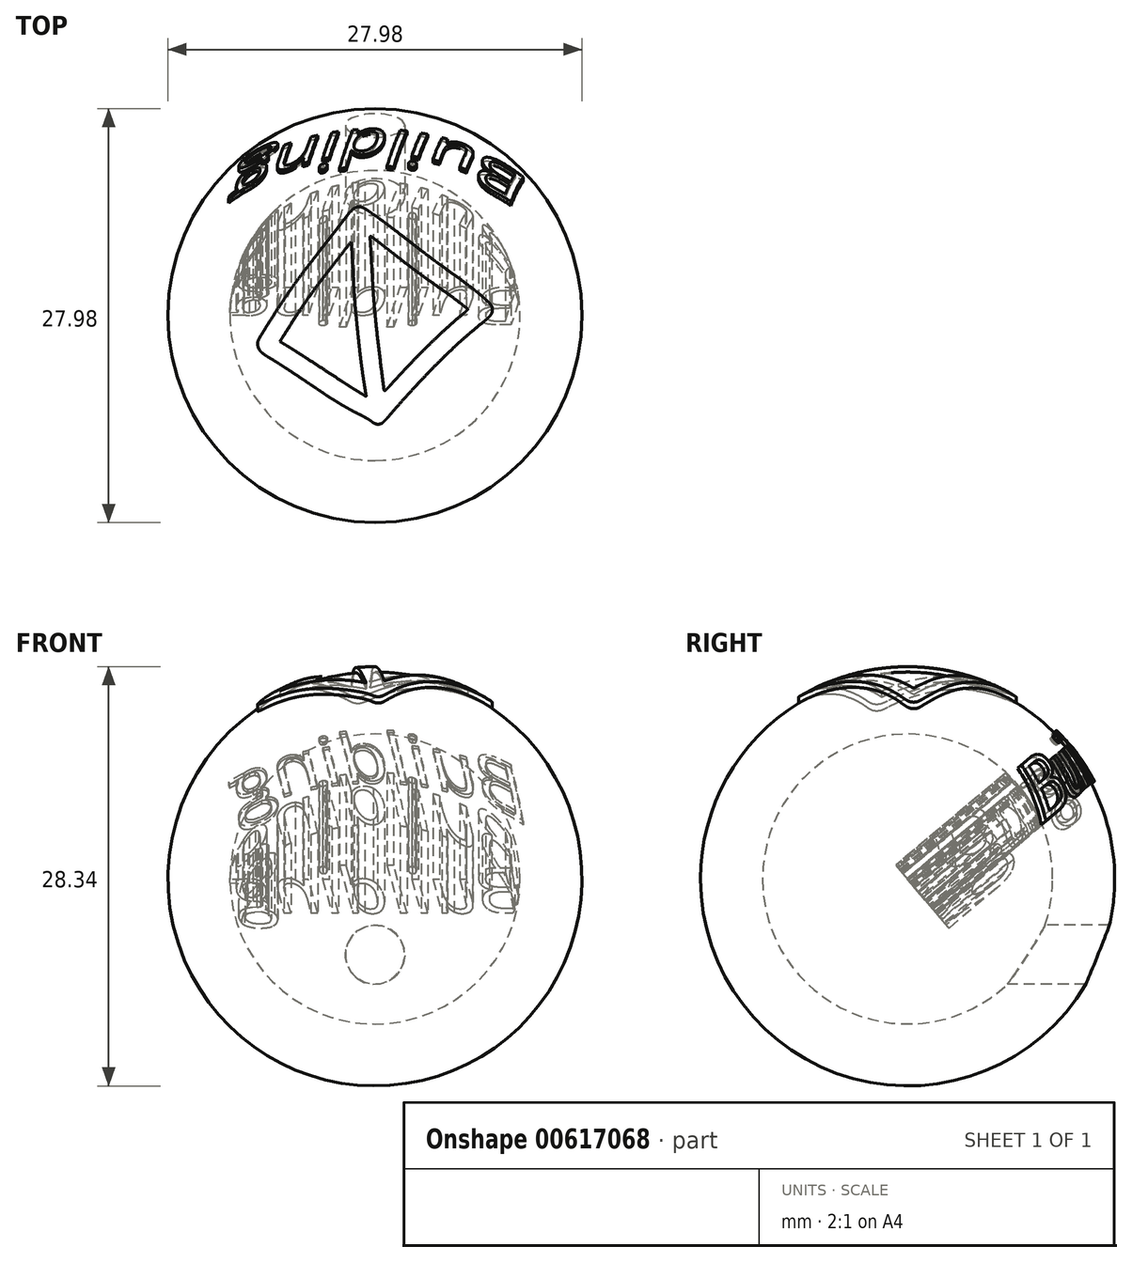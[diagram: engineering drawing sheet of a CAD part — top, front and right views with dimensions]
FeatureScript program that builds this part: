
annotation { "Feature Type Name" : "Feature", "Feature Type Description" : "" }
export const myFeature = defineFeature(function(context is Context, id is Id, definition is map)
    precondition{}
    {
        {
            var Q0;
            Q0=qCreatedBy(makeId("Top.planeOp"),FACE);
            var sketch = newSketch(context, id + "F0", { "sketchPlane" : qUnion([Q0])});
            skLineSegment(sketch, "E0", {"start": v(0, -10) * mm, "end": v(0, 10) * mm});
            skArc(sketch, "E1", {"start": v(0, 10) * mm, "mid": v(-10, 0) * mm, "end": v(0, -10) * mm});
            skSolve(sketch);
        }
        {
            var Q0;
            {var subQ0=sQuery(id+"F0.wireOp",EDGE,"E1");Q0=makeQuery(id+"F0.imprint","IMPRINT",FACE,{"disambiguationData":[TD([[makeQuery(id+"F0.imprint","IMPRINT",EDGE,{"derivedFrom":subQ0}),1.0]])]});}
            var Q1;
            Q1=sQuery(id+"F0.wireOp",EDGE,"E0");
            revolve(context, id + "F1", {"entities" : qUnion([Q0]), "axis" : qUnion([Q1]), "revolveType" : RevolveType.FULL});
        }
        {
            var Q0;
            Q0=makeQuery(id+"F1.opRevolve","SWEPT_BODY",BODY,{"disambiguationData":[OSD([sQuery(id+"F0.wireOp",EDGE,"E0"),sQuery(id+"F0.wireOp",EDGE,"E1")])]});
            var Q1;
            Q1=sQuery(id+"F0.wireOp",VERTEX,"NPe4G0ez-t7S9-9isL-QO5v-uuJu600mHcIT.center");
            var Q2;
            Q2=sQuery(id+"F0.wireOp",VERTEX,"E1.center");
            transform(context, id + "F2", {"entities" : qUnion([Q0]), "transformType" : TransformType.SCALE_UNIFORMLY, "scale" : 33.3, "scalePoint" : qUnion([Q2]), "makeCopy" : false});
        }
        {
            var Q0;
            Q0=qCreatedBy(makeId("Top.planeOp"),FACE);
            var sketch = newSketch(context, id + "F3", { "sketchPlane" : qUnion([Q0])});
            skArc(sketch, "E2", {"start": v(-33, 172.81) * mm, "mid": v(-34.37, 171.98) * mm, "end": v(-35.66, 171) * mm});
            skArc(sketch, "E3", {"start": v(-35.66, 171) * mm, "mid": v(-37.15, 169.67) * mm, "end": v(-38.56, 168.26) * mm});
            skArc(sketch, "E4", {"start": v(-38.56, 168.26) * mm, "mid": v(-40.37, 166.25) * mm, "end": v(-42.1, 164.18) * mm});
            skArc(sketch, "E5", {"start": v(-42.1, 164.18) * mm, "mid": v(-44.55, 161.1) * mm, "end": v(-46.95, 157.98) * mm});
            skArc(sketch, "E6", {"start": v(-46.95, 157.98) * mm, "mid": v(-49.6, 154.52) * mm, "end": v(-52.25, 151.08) * mm});
            skArc(sketch, "E7", {"start": v(-52.25, 151.08) * mm, "mid": v(-56.88, 145.1) * mm, "end": v(-61.52, 139.12) * mm});
            skArc(sketch, "E8", {"start": v(-61.52, 139.12) * mm, "mid": v(-66.9, 132.2) * mm, "end": v(-72.28, 125.28) * mm});
            skArc(sketch, "E9", {"start": v(-72.28, 125.28) * mm, "mid": v(-77.76, 118.26) * mm, "end": v(-83.25, 111.24) * mm});
            skArc(sketch, "E10", {"start": v(-83.25, 111.24) * mm, "mid": v(-97.95, 92.31) * mm, "end": v(-112.54, 73.3) * mm});
            skArc(sketch, "E11", {"start": v(-112.54, 73.3) * mm, "mid": v(-122.82, 59.57) * mm, "end": v(-132.87, 45.67) * mm});
            skArc(sketch, "E12", {"start": v(-132.87, 45.67) * mm, "mid": v(-142, 32.54) * mm, "end": v(-150.9, 19.25) * mm});
            skArc(sketch, "E13", {"start": v(-150.9, 19.25) * mm, "mid": v(-161.66, 2.63) * mm, "end": v(-172.26, -14.1) * mm});
            skArc(sketch, "E14", {"start": v(-172.26, -14.1) * mm, "mid": v(-177.97, -23.22) * mm, "end": v(-183.64, -32.36) * mm});
            skArc(sketch, "E15", {"start": v(-183.64, -32.36) * mm, "mid": v(-185.48, -35.48) * mm, "end": v(-187.18, -38.67) * mm});
            skArc(sketch, "E16", {"start": v(-187.18, -38.67) * mm, "mid": v(-188, -40.65) * mm, "end": v(-188.56, -42.72) * mm});
            skArc(sketch, "E17", {"start": v(-188.56, -42.72) * mm, "mid": v(-188.82, -44.8) * mm, "end": v(-188.77, -46.88) * mm});
            skArc(sketch, "E18", {"start": v(-188.77, -46.88) * mm, "mid": v(-188.23, -49.88) * mm, "end": v(-187.2, -52.73) * mm});
            skArc(sketch, "E19", {"start": v(-187.2, -52.73) * mm, "mid": v(-185.68, -55.44) * mm, "end": v(-183.75, -57.87) * mm});
            skArc(sketch, "E20", {"start": v(-183.75, -57.87) * mm, "mid": v(-180.92, -60.6) * mm, "end": v(-177.8, -63) * mm});
            skArc(sketch, "E21", {"start": v(-177.8, -63) * mm, "mid": v(-173.08, -66.1) * mm, "end": v(-168.25, -69) * mm});
            skArc(sketch, "E22", {"start": v(-168.25, -69) * mm, "mid": v(-164.73, -71.07) * mm, "end": v(-161.26, -73.21) * mm});
            skArc(sketch, "E23", {"start": v(-161.26, -73.21) * mm, "mid": v(-155.32, -76.99) * mm, "end": v(-149.4, -80.79) * mm});
            skArc(sketch, "E24", {"start": v(-149.4, -80.79) * mm, "mid": v(-142.56, -85.22) * mm, "end": v(-135.75, -89.69) * mm});
            skArc(sketch, "E25", {"start": v(-135.75, -89.69) * mm, "mid": v(-128.86, -94.25) * mm, "end": v(-122, -98.84) * mm});
            skArc(sketch, "E26", {"start": v(-122, -98.84) * mm, "mid": v(-115.2, -103.41) * mm, "end": v(-108.4, -107.98) * mm});
            skArc(sketch, "E27", {"start": v(-108.4, -107.98) * mm, "mid": v(-101.82, -112.4) * mm, "end": v(-95.25, -116.8) * mm});
            skArc(sketch, "E28", {"start": v(-95.25, -116.8) * mm, "mid": v(-89.63, -120.57) * mm, "end": v(-84.02, -124.33) * mm});
            skArc(sketch, "E29", {"start": v(-84.02, -124.33) * mm, "mid": v(-81, -126.34) * mm, "end": v(-78, -128.35) * mm});
            skArc(sketch, "E30", {"start": v(-78, -128.35) * mm, "mid": v(-71.4, -132.67) * mm, "end": v(-64.72, -136.88) * mm});
            skArc(sketch, "E31", {"start": v(-64.72, -136.88) * mm, "mid": v(-57.8, -141.12) * mm, "end": v(-50.8, -145.26) * mm});
            skArc(sketch, "E32", {"start": v(-50.8, -145.26) * mm, "mid": v(-44.03, -149.14) * mm, "end": v(-37.21, -152.92) * mm});
            skArc(sketch, "E33", {"start": v(-37.21, -152.92) * mm, "mid": v(-31.14, -156.15) * mm, "end": v(-25, -159.25) * mm});
            skArc(sketch, "E34", {"start": v(-25, -159.25) * mm, "mid": v(-22.06, -160.7) * mm, "end": v(-19.16, -162.22) * mm});
            skArc(sketch, "E35", {"start": v(-19.16, -162.22) * mm, "mid": v(-16.38, -163.71) * mm, "end": v(-13.63, -165.25) * mm});
            skArc(sketch, "E36", {"start": v(-13.63, -165.25) * mm, "mid": v(-11.31, -166.6) * mm, "end": v(-9.01, -168) * mm});
            skArc(sketch, "E37", {"start": v(-9.01, -168) * mm, "mid": v(-7.81, -168.8) * mm, "end": v(-6.69, -169.7) * mm});
            skArc(sketch, "E38", {"start": v(-6.69, -169.7) * mm, "mid": v(-4.48, -171.46) * mm, "end": v(-2.12, -173) * mm});
            skArc(sketch, "E39", {"start": v(-2.12, -173) * mm, "mid": v(0.04, -174.03) * mm, "end": v(2.34, -174.72) * mm});
            skArc(sketch, "E40", {"start": v(2.34, -174.72) * mm, "mid": v(4.5, -174.99) * mm, "end": v(6.69, -174.86) * mm});
            skArc(sketch, "E41", {"start": v(6.69, -174.86) * mm, "mid": v(8.87, -174.35) * mm, "end": v(10.94, -173.5) * mm});
            skArc(sketch, "E42", {"start": v(10.94, -173.5) * mm, "mid": v(11.75, -173) * mm, "end": v(12.5, -172.4) * mm});
            skArc(sketch, "E43", {"start": v(12.5, -172.4) * mm, "mid": v(13.95, -171) * mm, "end": v(15.38, -169.59) * mm});
            skArc(sketch, "E44", {"start": v(15.38, -169.59) * mm, "mid": v(17.06, -167.86) * mm, "end": v(18.7, -166.1) * mm});
            skArc(sketch, "E45", {"start": v(18.7, -166.1) * mm, "mid": v(20.42, -164.19) * mm, "end": v(22.1, -162.24) * mm});
            skArc(sketch, "E46", {"start": v(22.1, -162.24) * mm, "mid": v(32.46, -150.21) * mm, "end": v(42.96, -138.3) * mm});
            skArc(sketch, "E47", {"start": v(42.96, -138.3) * mm, "mid": v(54.31, -125.7) * mm, "end": v(65.78, -113.23) * mm});
            skArc(sketch, "E48", {"start": v(65.78, -113.23) * mm, "mid": v(77.16, -101.09) * mm, "end": v(88.65, -89.06) * mm});
            skArc(sketch, "E49", {"start": v(88.65, -89.06) * mm, "mid": v(99.07, -78.41) * mm, "end": v(109.64, -67.9) * mm});
            skArc(sketch, "E50", {"start": v(109.64, -67.9) * mm, "mid": v(117.81, -59.96) * mm, "end": v(126.06, -52.09) * mm});
            skArc(sketch, "E51", {"start": v(126.06, -52.09) * mm, "mid": v(133.02, -45.6) * mm, "end": v(140.08, -39.23) * mm});
            skArc(sketch, "E52", {"start": v(140.08, -39.23) * mm, "mid": v(147.61, -32.64) * mm, "end": v(155.23, -26.15) * mm});
            skArc(sketch, "E53", {"start": v(155.23, -26.15) * mm, "mid": v(165.3, -17.77) * mm, "end": v(175.42, -9.46) * mm});
            skArc(sketch, "E54", {"start": v(175.42, -9.46) * mm, "mid": v(179.05, -6.39) * mm, "end": v(182.58, -3.2) * mm});
            skArc(sketch, "E55", {"start": v(182.58, -3.2) * mm, "mid": v(184.71, -0.94) * mm, "end": v(186.58, 1.54) * mm});
            skArc(sketch, "E56", {"start": v(186.58, 1.54) * mm, "mid": v(187.71, 3.63) * mm, "end": v(188.46, 5.89) * mm});
            skArc(sketch, "E57", {"start": v(188.46, 5.89) * mm, "mid": v(188.81, 8.25) * mm, "end": v(188.75, 10.64) * mm});
            skArc(sketch, "E58", {"start": v(188.75, 10.64) * mm, "mid": v(188.42, 12.49) * mm, "end": v(187.86, 14.28) * mm});
            skArc(sketch, "E59", {"start": v(187.86, 14.28) * mm, "mid": v(187.09, 15.92) * mm, "end": v(186.1, 17.44) * mm});
            skArc(sketch, "E60", {"start": v(186.1, 17.44) * mm, "mid": v(184.48, 19.41) * mm, "end": v(182.72, 21.24) * mm});
            skArc(sketch, "E61", {"start": v(182.72, 21.24) * mm, "mid": v(179.3, 24.49) * mm, "end": v(175.84, 27.68) * mm});
            skArc(sketch, "E62", {"start": v(175.84, 27.68) * mm, "mid": v(171.1, 31.88) * mm, "end": v(166.27, 35.95) * mm});
            skArc(sketch, "E63", {"start": v(166.27, 35.95) * mm, "mid": v(160.23, 40.83) * mm, "end": v(154.12, 45.63) * mm});
            skArc(sketch, "E64", {"start": v(154.12, 45.63) * mm, "mid": v(146.93, 51.13) * mm, "end": v(139.67, 56.53) * mm});
            skArc(sketch, "E65", {"start": v(139.67, 56.53) * mm, "mid": v(131.36, 62.6) * mm, "end": v(123, 68.58) * mm});
            skArc(sketch, "E66", {"start": v(123, 68.58) * mm, "mid": v(114.4, 74.72) * mm, "end": v(105.83, 80.91) * mm});
            skArc(sketch, "E67", {"start": v(105.83, 80.91) * mm, "mid": v(98.5, 86.27) * mm, "end": v(91.21, 91.69) * mm});
            skArc(sketch, "E68", {"start": v(91.21, 91.69) * mm, "mid": v(83.18, 97.75) * mm, "end": v(75.19, 103.87) * mm});
            skArc(sketch, "E69", {"start": v(75.19, 103.87) * mm, "mid": v(64.09, 112.45) * mm, "end": v(53, 121.05) * mm});
            skArc(sketch, "E70", {"start": v(53, 121.05) * mm, "mid": v(42.99, 128.83) * mm, "end": v(32.94, 136.58) * mm});
            skArc(sketch, "E71", {"start": v(32.94, 136.58) * mm, "mid": v(25.36, 142.38) * mm, "end": v(17.73, 148.12) * mm});
            skArc(sketch, "E72", {"start": v(17.73, 148.12) * mm, "mid": v(11.29, 152.88) * mm, "end": v(4.8, 157.6) * mm});
            skArc(sketch, "E73", {"start": v(4.8, 157.6) * mm, "mid": v(-1.5, 162.08) * mm, "end": v(-7.86, 166.51) * mm});
            skArc(sketch, "E74", {"start": v(-7.86, 166.51) * mm, "mid": v(-12.3, 169.46) * mm, "end": v(-16.82, 172.26) * mm});
            skArc(sketch, "E75", {"start": v(-16.82, 172.26) * mm, "mid": v(-19.64, 173.67) * mm, "end": v(-22.64, 174.66) * mm});
            skArc(sketch, "E76", {"start": v(-22.64, 174.66) * mm, "mid": v(-25.1, 175) * mm, "end": v(-27.56, 174.77) * mm});
            skArc(sketch, "E77", {"start": v(-27.56, 174.77) * mm, "mid": v(-30.35, 173.98) * mm, "end": v(-33, 172.81) * mm});
            skArc(sketch, "E78", {"start": v(2.5, 120.65) * mm, "mid": v(4.7, 119) * mm, "end": v(6.88, 117.32) * mm});
            skArc(sketch, "E79", {"start": v(6.88, 117.32) * mm, "mid": v(10.53, 114.5) * mm, "end": v(14.18, 111.67) * mm});
            skArc(sketch, "E80", {"start": v(14.18, 111.67) * mm, "mid": v(18.38, 108.4) * mm, "end": v(22.57, 105.14) * mm});
            skArc(sketch, "E81", {"start": v(22.57, 105.14) * mm, "mid": v(26.8, 101.84) * mm, "end": v(31, 98.53) * mm});
            skArc(sketch, "E82", {"start": v(31, 98.53) * mm, "mid": v(40.47, 91.14) * mm, "end": v(49.96, 83.78) * mm});
            skArc(sketch, "E83", {"start": v(49.96, 83.78) * mm, "mid": v(57.43, 78.07) * mm, "end": v(64.95, 72.41) * mm});
            skArc(sketch, "E84", {"start": v(64.95, 72.41) * mm, "mid": v(72.33, 66.96) * mm, "end": v(79.75, 61.57) * mm});
            skArc(sketch, "E85", {"start": v(79.75, 61.57) * mm, "mid": v(88.87, 55.05) * mm, "end": v(98, 48.58) * mm});
            skArc(sketch, "E86", {"start": v(98, 48.58) * mm, "mid": v(108.94, 40.81) * mm, "end": v(119.82, 32.97) * mm});
            skArc(sketch, "E87", {"start": v(119.82, 32.97) * mm, "mid": v(127.9, 27) * mm, "end": v(135.87, 20.91) * mm});
            skArc(sketch, "E88", {"start": v(135.87, 20.91) * mm, "mid": v(142.08, 16.05) * mm, "end": v(148.26, 11.14) * mm});
            skArc(sketch, "E89", {"start": v(148.26, 11.14) * mm, "mid": v(148.87, 10.2) * mm, "end": v(148.8, 9.07) * mm});
            skArc(sketch, "E90", {"start": v(148.8, 9.07) * mm, "mid": v(148.66, 8.82) * mm, "end": v(148.47, 8.6) * mm});
            skArc(sketch, "E91", {"start": v(148.47, 8.6) * mm, "mid": v(147.14, 7.42) * mm, "end": v(145.8, 6.25) * mm});
            skArc(sketch, "E92", {"start": v(145.8, 6.25) * mm, "mid": v(144.24, 4.89) * mm, "end": v(142.67, 3.54) * mm});
            skArc(sketch, "E93", {"start": v(142.67, 3.54) * mm, "mid": v(140.84, 2) * mm, "end": v(139, 0.47) * mm});
            skArc(sketch, "E94", {"start": v(139, 0.47) * mm, "mid": v(126.28, -10.36) * mm, "end": v(113.83, -21.52) * mm});
            skArc(sketch, "E95", {"start": v(113.83, -21.52) * mm, "mid": v(99.63, -34.82) * mm, "end": v(85.65, -48.36) * mm});
            skArc(sketch, "E96", {"start": v(85.65, -48.36) * mm, "mid": v(70.67, -63.33) * mm, "end": v(55.94, -78.53) * mm});
            skArc(sketch, "E97", {"start": v(55.94, -78.53) * mm, "mid": v(40.89, -94.52) * mm, "end": v(26.07, -110.7) * mm});
            skArc(sketch, "E98", {"start": v(26.07, -110.7) * mm, "mid": v(24.28, -112.68) * mm, "end": v(22.47, -114.64) * mm});
            skArc(sketch, "E99", {"start": v(22.47, -114.64) * mm, "mid": v(20.9, -116.3) * mm, "end": v(19.32, -117.95) * mm});
            skArc(sketch, "E100", {"start": v(19.32, -117.95) * mm, "mid": v(17.95, -119.36) * mm, "end": v(16.56, -120.76) * mm});
            skArc(sketch, "E101", {"start": v(16.56, -120.76) * mm, "mid": v(16.35, -120.9) * mm, "end": v(16.1, -120.96) * mm});
            skArc(sketch, "E102", {"start": v(16.1, -120.96) * mm, "mid": v(14.93, -120.52) * mm, "end": v(14.34, -119.42) * mm});
            skArc(sketch, "E103", {"start": v(14.34, -119.42) * mm, "mid": v(11.4, -96.18) * mm, "end": v(8.47, -72.95) * mm});
            skArc(sketch, "E104", {"start": v(8.47, -72.95) * mm, "mid": v(5.63, -49.46) * mm, "end": v(2.99, -25.95) * mm});
            skArc(sketch, "E105", {"start": v(2.99, -25.95) * mm, "mid": v(0.67, -3.46) * mm, "end": v(-1.44, 19.04) * mm});
            skArc(sketch, "E106", {"start": v(-1.44, 19.04) * mm, "mid": v(-1.82, 23.65) * mm, "end": v(-2.17, 28.26) * mm});
            skArc(sketch, "E107", {"start": v(-2.17, 28.26) * mm, "mid": v(-2.65, 35.41) * mm, "end": v(-3.12, 42.56) * mm});
            skArc(sketch, "E108", {"start": v(-3.12, 42.56) * mm, "mid": v(-3.62, 50.64) * mm, "end": v(-4.1, 58.71) * mm});
            skArc(sketch, "E109", {"start": v(-4.1, 58.71) * mm, "mid": v(-4.55, 66.63) * mm, "end": v(-4.98, 74.54) * mm});
            skArc(sketch, "E110", {"start": v(-4.98, 74.54) * mm, "mid": v(-5.38, 82.1) * mm, "end": v(-5.8, 89.67) * mm});
            skArc(sketch, "E111", {"start": v(-5.8, 89.67) * mm, "mid": v(-6.18, 96.69) * mm, "end": v(-6.58, 103.7) * mm});
            skArc(sketch, "E112", {"start": v(-6.58, 103.7) * mm, "mid": v(-6.92, 109.59) * mm, "end": v(-7.27, 115.47) * mm});
            skArc(sketch, "E113", {"start": v(-7.27, 115.47) * mm, "mid": v(-7.43, 117.96) * mm, "end": v(-7.62, 120.44) * mm});
            skArc(sketch, "E114", {"start": v(-7.62, 120.44) * mm, "mid": v(-7.85, 123.46) * mm, "end": v(-8.01, 126.48) * mm});
            skArc(sketch, "E115", {"start": v(-8.01, 126.48) * mm, "mid": v(-7.8, 127.05) * mm, "end": v(-7.26, 127.3) * mm});
            skArc(sketch, "E116", {"start": v(-7.26, 127.3) * mm, "mid": v(-6.45, 127.17) * mm, "end": v(-5.73, 126.8) * mm});
            skArc(sketch, "E117", {"start": v(-5.73, 126.8) * mm, "mid": v(-1.6, 123.74) * mm, "end": v(2.5, 120.65) * mm});
            skArc(sketch, "E118", {"start": v(-35.55, 75.04) * mm, "mid": v(-34.77, 59.8) * mm, "end": v(-33.94, 44.56) * mm});
            skArc(sketch, "E119", {"start": v(-33.94, 44.56) * mm, "mid": v(-33.32, 34.26) * mm, "end": v(-32.6, 23.96) * mm});
            skArc(sketch, "E120", {"start": v(-32.6, 23.96) * mm, "mid": v(-31.84, 14.28) * mm, "end": v(-30.97, 4.61) * mm});
            skArc(sketch, "E121", {"start": v(-30.97, 4.61) * mm, "mid": v(-29.73, -8.18) * mm, "end": v(-28.43, -20.96) * mm});
            skArc(sketch, "E122", {"start": v(-28.43, -20.96) * mm, "mid": v(-26.87, -35.75) * mm, "end": v(-25.25, -50.53) * mm});
            skArc(sketch, "E123", {"start": v(-25.25, -50.53) * mm, "mid": v(-23.89, -62.47) * mm, "end": v(-22.44, -74.39) * mm});
            skArc(sketch, "E124", {"start": v(-22.44, -74.39) * mm, "mid": v(-21.14, -84.39) * mm, "end": v(-19.77, -94.38) * mm});
            skArc(sketch, "E125", {"start": v(-19.77, -94.38) * mm, "mid": v(-18.47, -103.17) * mm, "end": v(-17.06, -111.95) * mm});
            skArc(sketch, "E126", {"start": v(-17.06, -111.95) * mm, "mid": v(-16.5, -115.31) * mm, "end": v(-15.96, -118.68) * mm});
            skArc(sketch, "E127", {"start": v(-15.96, -118.68) * mm, "mid": v(-15.5, -121.53) * mm, "end": v(-15.07, -124.38) * mm});
            skArc(sketch, "E128", {"start": v(-15.07, -124.38) * mm, "mid": v(-14.7, -126.92) * mm, "end": v(-14.32, -129.45) * mm});
            skArc(sketch, "E129", {"start": v(-14.32, -129.45) * mm, "mid": v(-14.33, -129.58) * mm, "end": v(-14.4, -129.7) * mm});
            skArc(sketch, "E130", {"start": v(-14.4, -129.7) * mm, "mid": v(-14.77, -129.88) * mm, "end": v(-15.17, -129.79) * mm});
            skArc(sketch, "E131", {"start": v(-15.17, -129.79) * mm, "mid": v(-21.77, -125.75) * mm, "end": v(-28.36, -121.71) * mm});
            skArc(sketch, "E132", {"start": v(-28.36, -121.71) * mm, "mid": v(-35.1, -117.53) * mm, "end": v(-41.81, -113.3) * mm});
            skArc(sketch, "E133", {"start": v(-41.81, -113.3) * mm, "mid": v(-48.42, -109.06) * mm, "end": v(-55, -104.77) * mm});
            skArc(sketch, "E134", {"start": v(-55, -104.77) * mm, "mid": v(-69.13, -95.47) * mm, "end": v(-83.29, -86.18) * mm});
            skArc(sketch, "E135", {"start": v(-83.29, -86.18) * mm, "mid": v(-95.7, -78.09) * mm, "end": v(-108.12, -70.02) * mm});
            skArc(sketch, "E136", {"start": v(-108.12, -70.02) * mm, "mid": v(-118.2, -63.5) * mm, "end": v(-128.3, -57.02) * mm});
            skArc(sketch, "E137", {"start": v(-128.3, -57.02) * mm, "mid": v(-134.23, -53.26) * mm, "end": v(-140.2, -49.57) * mm});
            skLineSegment(sketch, "E138", {"start": v(-140.2, -49.57) * mm, "end": v(-152.92, -41.82) * mm});
            skLineSegment(sketch, "E139", {"start": v(-152.92, -41.82) * mm, "end": v(-147.8, -33.64) * mm});
            skArc(sketch, "E140", {"start": v(-147.8, -33.64) * mm, "mid": v(-136.62, -15.94) * mm, "end": v(-125.26, 1.64) * mm});
            skArc(sketch, "E141", {"start": v(-125.26, 1.64) * mm, "mid": v(-115.72, 15.96) * mm, "end": v(-105.93, 30.11) * mm});
            skArc(sketch, "E142", {"start": v(-105.93, 30.11) * mm, "mid": v(-95.68, 44.37) * mm, "end": v(-85.19, 58.46) * mm});
            skArc(sketch, "E143", {"start": v(-85.19, 58.46) * mm, "mid": v(-71.73, 76.03) * mm, "end": v(-58.12, 93.49) * mm});
            skLineSegment(sketch, "E144", {"start": v(-58.12, 93.49) * mm, "end": v(-38.5, 118.44) * mm});
            skLineSegment(sketch, "E145", {"start": v(-38.5, 118.44) * mm, "end": v(-37.83, 112.99) * mm});
            skArc(sketch, "E146", {"start": v(-37.83, 112.99) * mm, "mid": v(-37.63, 111.2) * mm, "end": v(-37.5, 109.4) * mm});
            skArc(sketch, "E147", {"start": v(-37.5, 109.4) * mm, "mid": v(-37.18, 104.5) * mm, "end": v(-36.88, 99.6) * mm});
            skArc(sketch, "E148", {"start": v(-36.88, 99.6) * mm, "mid": v(-36.54, 93.74) * mm, "end": v(-36.22, 87.89) * mm});
            skArc(sketch, "E149", {"start": v(-36.22, 87.89) * mm, "mid": v(-35.88, 81.47) * mm, "end": v(-35.55, 75.04) * mm});
            skSolve(sketch);
        }
        {
            var Q0;
            Q0=qSketchRegion(id+"F3",true);
            var Q1;
            Q1=sQuery(id+"F3.wireOp",EDGE,"c928f899-12af-4b01-b412-b3b7da3d830f");
            var Q2;
            Q2=sQuery(id+"F3.wireOp",EDGE,"b69f99c7-a6d0-4d1b-8752-9e82ab4c99ec");
            extrude(context, id + "F4", {"entities" : qUnion([Q0]), "operationType" : NewBodyOperationType.ADD, "surfaceEntities" : qUnion([Q1, Q2]), "depth" : 350 * mm});
        }
        {
            var Q0;
            Q0=makeQuery(id+"F4.opExtrude","SWEPT_BODY",BODY,{"disambiguationData":[OSD([sQuery(id+"F3.wireOp",EDGE,"15c6da4e-992d-4824-9d20-70d2d6be9970"),sQuery(id+"F3.wireOp",EDGE,"268c69ec-46be-456f-85eb-69decc32fe39"),sQuery(id+"F3.wireOp",EDGE,"1d386307-6059-4203-bca6-0c1cec3c82e1"),sQuery(id+"F3.wireOp",EDGE,"7d7c66d2-f869-427f-806b-ad436cacd60e"),sQuery(id+"F3.wireOp",EDGE,"1db91850-860e-493f-a3af-7a0f3f1512ae"),sQuery(id+"F3.wireOp",EDGE,"2c65f23b-9f03-4f6f-ab37-de452af29e3c"),sQuery(id+"F3.wireOp",EDGE,"ba006cbc-bbd7-44d9-84cc-9cde0967c280"),sQuery(id+"F3.wireOp",EDGE,"ae950208-c781-4a25-8fcf-ffe59b9085ff"),sQuery(id+"F3.wireOp",EDGE,"3cce0944-c62d-4831-9b9d-d1a418d328b4"),sQuery(id+"F3.wireOp",EDGE,"9edc5e7d-16c0-40c4-98ad-6b91d5df0e78"),sQuery(id+"F3.wireOp",EDGE,"aa452f44-44a2-4c64-bff5-a2a639df00db"),sQuery(id+"F3.wireOp",EDGE,"16259f99-ce20-4b7b-81e1-fa0909c03eb4"),sQuery(id+"F3.wireOp",EDGE,"79895566-a943-429d-b257-d76af3645bdf"),sQuery(id+"F3.wireOp",EDGE,"a85490ef-f17e-45c8-b92b-28215162778a"),sQuery(id+"F3.wireOp",EDGE,"322f1036-a6fd-4992-ab69-5919540af7a6"),sQuery(id+"F3.wireOp",EDGE,"0a87ff38-4ab4-4140-b3c3-2d7501d9f3b1"),sQuery(id+"F3.wireOp",EDGE,"a6e7bdf2-ef3e-49d4-9b3c-e34f5a41e0c4"),sQuery(id+"F3.wireOp",EDGE,"3e588790-576f-47c1-9730-f5e27fa1e8f9"),sQuery(id+"F3.wireOp",EDGE,"ce3739ef-15fd-4754-ad9c-ccf511a9a8fb"),sQuery(id+"F3.wireOp",EDGE,"201134a3-66f3-4a3f-aa9b-76948966efc0"),sQuery(id+"F3.wireOp",EDGE,"65b511ea-0759-428d-8070-88e1f521d8ea"),sQuery(id+"F3.wireOp",EDGE,"c37cddb6-5cf8-4891-aff4-7191a72080b9"),sQuery(id+"F3.wireOp",EDGE,"52a43dbd-e952-43e1-be3d-d70e107260e6"),sQuery(id+"F3.wireOp",EDGE,"08c1271f-f5c3-4f26-be27-7f5e21217dff"),sQuery(id+"F3.wireOp",EDGE,"59a09f58-0503-4180-962a-e04db21f0da8"),sQuery(id+"F3.wireOp",EDGE,"e56a4626-e956-42c3-bb5d-cd9dae1ca801"),sQuery(id+"F3.wireOp",EDGE,"5ff5d55f-af90-49eb-8040-353101557de8"),sQuery(id+"F3.wireOp",EDGE,"0ed7430b-e164-4f56-8af9-4534524aa7c0"),sQuery(id+"F3.wireOp",EDGE,"b5610a6e-b6bb-43e3-9a8d-d3d7c5f0098b"),sQuery(id+"F3.wireOp",EDGE,"1d417af8-88ad-47c2-a4e2-6fec82bd6695"),sQuery(id+"F3.wireOp",EDGE,"778ae99a-956a-4ddb-8078-d9bc57f9fc8e"),sQuery(id+"F3.wireOp",EDGE,"5b19af09-f144-446e-9dfa-8766819c9efd"),sQuery(id+"F3.wireOp",EDGE,"028339f6-0475-4a57-af8d-550e32ad7466"),sQuery(id+"F3.wireOp",EDGE,"d5ae35b6-d210-433a-92c8-e92622696872"),sQuery(id+"F3.wireOp",EDGE,"16a2e606-2caa-4876-9ffa-8f08c4ff3a37"),sQuery(id+"F3.wireOp",EDGE,"5b90b144-be56-4de7-a9dd-c1e0336acbe3"),sQuery(id+"F3.wireOp",EDGE,"5912d126-c5fc-41e4-bfb8-b4fefc52ca72"),sQuery(id+"F3.wireOp",EDGE,"2e96ce95-bd3e-4f27-a7f8-b62cf5efe954"),sQuery(id+"F3.wireOp",EDGE,"ecb4e259-1207-4dd0-bc3c-87c6506cc3a5"),sQuery(id+"F3.wireOp",EDGE,"105fb72e-4d79-4204-af2f-b3b26f5eb8d1"),sQuery(id+"F3.wireOp",EDGE,"fa59b598-df54-48c6-bb8f-c5f7618c69d0"),sQuery(id+"F3.wireOp",EDGE,"a6beef0d-f124-47ac-b957-e6cd3057a354"),sQuery(id+"F3.wireOp",EDGE,"7c3eaf53-dcb7-43b1-ad18-80ff953eb59e"),sQuery(id+"F3.wireOp",EDGE,"281fe206-104f-408f-94b6-be79f12604c9")])]});
            var Q1;
            Q1=makeQuery(id+"F4.opExtrude","SWEPT_BODY",BODY,{"disambiguationData":[OSD([sQuery(id+"F3.wireOp",EDGE,"58f6206a-5554-41d4-8cf7-6e0b4724a469"),sQuery(id+"F3.wireOp",EDGE,"85dabe77-b6aa-43d5-a519-64383616f71e"),sQuery(id+"F3.wireOp",EDGE,"4b679fe6-9e11-497d-b8fd-14ca14e49ddd"),sQuery(id+"F3.wireOp",EDGE,"51de25f6-d59e-4805-a327-1fd7e38869c8"),sQuery(id+"F3.wireOp",EDGE,"d47977fb-70d3-4df8-bc35-66fcc0e556e0"),sQuery(id+"F3.wireOp",EDGE,"235006b0-8f14-4ca2-82f0-f96b6b8c4766"),sQuery(id+"F3.wireOp",EDGE,"0fc7acd6-1c1d-47a8-ba12-62eb658d35ca"),sQuery(id+"F3.wireOp",EDGE,"883fa5e3-ca4c-4ce6-a249-4debf538fe24"),sQuery(id+"F3.wireOp",EDGE,"1da09ed1-22d9-43a1-a655-8acff5d61309"),sQuery(id+"F3.wireOp",EDGE,"32654a82-a09a-444f-bf73-45f818f0f235"),sQuery(id+"F3.wireOp",EDGE,"a398fd80-a0a9-4724-ba0e-1a7a000baa92"),sQuery(id+"F3.wireOp",EDGE,"f39f97c8-53f5-4046-9905-b28daecd4f10"),sQuery(id+"F3.wireOp",EDGE,"2484d883-0ec2-4c7d-9023-165ebbef226c"),sQuery(id+"F3.wireOp",EDGE,"f026d96f-3d32-4113-a1c9-3545f5cdbe4a"),sQuery(id+"F3.wireOp",EDGE,"974fee18-719e-4620-aace-d3676da2011b"),sQuery(id+"F3.wireOp",EDGE,"0c5766d2-a026-45af-bffd-0d1f783d5157"),sQuery(id+"F3.wireOp",EDGE,"5da13fee-9c04-45d8-805f-c7a03dde2383"),sQuery(id+"F3.wireOp",EDGE,"dbea32a3-85bd-4957-aef2-b6fe64a02f6b"),sQuery(id+"F3.wireOp",EDGE,"fba134ea-bf40-4191-ad8f-cc6b2b040a97"),sQuery(id+"F3.wireOp",EDGE,"0c19e200-7cd5-4fcb-83ed-261bd7936bc7"),sQuery(id+"F3.wireOp",EDGE,"246b843b-ea86-44e5-9cb9-335e6677b61d"),sQuery(id+"F3.wireOp",EDGE,"c1b3c9bc-1eb4-4c9b-99c8-0cebed89395a"),sQuery(id+"F3.wireOp",EDGE,"f93eebc3-1447-4029-8362-91325193ac2b"),sQuery(id+"F3.wireOp",EDGE,"bf86b12d-53a9-4c19-abaa-b1e658933ceb"),sQuery(id+"F3.wireOp",EDGE,"89646a71-1a60-4e14-b80a-74fb601d0855"),sQuery(id+"F3.wireOp",EDGE,"7b03dcde-0a52-4f3c-80e9-110d1d805e93"),sQuery(id+"F3.wireOp",EDGE,"83e8d1f3-8820-485b-8b6d-3ecd79124883"),sQuery(id+"F3.wireOp",EDGE,"ec7b56eb-ca95-44fd-a774-e9b7f9d3f50d"),sQuery(id+"F3.wireOp",EDGE,"31861aa6-cfd1-43ce-a7c5-bacfb7e2a30f"),sQuery(id+"F3.wireOp",EDGE,"fa3de647-1dd9-4141-982b-74ae8d07851d"),sQuery(id+"F3.wireOp",EDGE,"75d7c1c5-761c-4178-bfd4-4f469045899b"),sQuery(id+"F3.wireOp",EDGE,"4b3d7518-bd5d-4ecc-b2c5-d8dd665de4f4"),sQuery(id+"F3.wireOp",EDGE,"3be2682d-01bd-4f31-9cde-9df16a01e4a9"),sQuery(id+"F3.wireOp",EDGE,"72d3c7a9-2794-46eb-9b0d-6c526cc1b9a3"),sQuery(id+"F3.wireOp",EDGE,"0137e336-6b26-4f8d-b9ad-47ce1aa9eb31"),sQuery(id+"F3.wireOp",EDGE,"96000e4a-2d86-4b9f-af7d-a1c875cc048c"),sQuery(id+"F3.wireOp",EDGE,"139c5a79-9c0f-4e15-b57f-4c09662495a3"),sQuery(id+"F3.wireOp",EDGE,"8ea04d8b-b3da-46bb-9742-d8cba6b23bda"),sQuery(id+"F3.wireOp",EDGE,"b352b580-467e-481c-88ac-6217b8462947"),sQuery(id+"F3.wireOp",EDGE,"2503a493-1722-4539-8d54-7329fc0b116a"),sQuery(id+"F3.wireOp",EDGE,"a0615e06-0a48-4c65-8818-f0f693937022"),sQuery(id+"F3.wireOp",EDGE,"08389002-1ce8-438a-b5a4-698ca33590c2"),sQuery(id+"F3.wireOp",EDGE,"1756e4aa-c30a-461e-962c-81ee35d31e55"),sQuery(id+"F3.wireOp",EDGE,"5f84c249-07ea-4efb-9be3-ca494937f772"),sQuery(id+"F3.wireOp",EDGE,"cbefd041-b54f-4587-87b6-437b2290d1fc"),sQuery(id+"F3.wireOp",EDGE,"d44f58d4-f1a7-4aec-b016-8e7f1e498aeb"),sQuery(id+"F3.wireOp",EDGE,"0a5be90b-7545-44ea-9f2d-c726a5a2121c"),sQuery(id+"F3.wireOp",EDGE,"0cfaa442-d102-4580-8ef6-489f2aa1e6b3")])]});
            var Q2;
            Q2=makeQuery(id+"F4.opExtrude","SWEPT_BODY",BODY,{"disambiguationData":[OSD([sQuery(id+"F3.wireOp",EDGE,"9cc7aec6-4d94-4577-ab6c-32f5aa316238"),sQuery(id+"F3.wireOp",EDGE,"5ab2d840-4a32-405a-8c4b-a8126e3e1bc1"),sQuery(id+"F3.wireOp",EDGE,"56de48b4-9620-4637-8196-310e2641530f"),sQuery(id+"F3.wireOp",EDGE,"55327826-e64b-4830-85f2-3f22d36f43b5"),sQuery(id+"F3.wireOp",EDGE,"0245b46f-a639-4a95-8ca3-1568736ceed2"),sQuery(id+"F3.wireOp",EDGE,"9bd8a002-6ca7-4c84-8984-a620eefad103"),sQuery(id+"F3.wireOp",EDGE,"d4736c5e-da0b-46a0-ba9d-17ae07bb2b66"),sQuery(id+"F3.wireOp",EDGE,"125695b8-77e6-4e99-8f78-5f8fae1a0c71"),sQuery(id+"F3.wireOp",EDGE,"c9f25b10-a495-4684-8f25-8f255fabab6e"),sQuery(id+"F3.wireOp",EDGE,"0dbee67a-2ab6-4abb-ae16-0fe64d623848"),sQuery(id+"F3.wireOp",EDGE,"92c08d8e-ed2e-41a3-9c1a-b5ddaf8a0bf1"),sQuery(id+"F3.wireOp",EDGE,"00fabb15-0c1e-492e-85c1-17390e5b12bc"),sQuery(id+"F3.wireOp",EDGE,"065a9352-dddb-4e3f-b02a-444c867b75fe"),sQuery(id+"F3.wireOp",EDGE,"ef206bb6-e4f2-4189-9fc7-a7823c329ad6"),sQuery(id+"F3.wireOp",EDGE,"7199cbbe-c9bf-4cb9-b928-2ff8a84eb09e"),sQuery(id+"F3.wireOp",EDGE,"17bf9ed1-b881-4f74-816d-3511b6b328c7"),sQuery(id+"F3.wireOp",EDGE,"e5b615d0-4193-495d-b285-bd69ae30f000"),sQuery(id+"F3.wireOp",EDGE,"cfeaf62f-6be1-426b-9732-01e1a667be7e"),sQuery(id+"F3.wireOp",EDGE,"ac56344b-5ee6-4fa5-8e47-65b2a4ea3a01"),sQuery(id+"F3.wireOp",EDGE,"45b5fa53-15fd-43a0-91b0-943cc3286fc9")])]});
            var Q3;
            Q3=makeQuery(id+"F4.opExtrude","SWEPT_BODY",BODY,{"disambiguationData":[OSD([sQuery(id+"F3.wireOp",EDGE,"7bdfe37d-9957-4663-8239-5490fd3220d9"),sQuery(id+"F3.wireOp",EDGE,"6a91314f-c002-4565-bbf8-bb9f29165fb8"),sQuery(id+"F3.wireOp",EDGE,"b69f99c7-a6d0-4d1b-8752-9e82ab4c99ec"),sQuery(id+"F3.wireOp",EDGE,"c928f899-12af-4b01-b412-b3b7da3d830f"),sQuery(id+"F3.wireOp",EDGE,"ffa58721-cdd5-406d-be26-d96f7a050df4"),sQuery(id+"F3.wireOp",EDGE,"02fc7fb8-293b-44ff-ab78-63506d0aedb9"),sQuery(id+"F3.wireOp",EDGE,"147fb6cb-2565-4fb5-9280-6afbf9eef36b"),sQuery(id+"F3.wireOp",EDGE,"2cee3704-4124-415a-b391-31af1cf305d7"),sQuery(id+"F3.wireOp",EDGE,"32b2fb71-03c8-4978-9d95-2b5aaf044d0d"),sQuery(id+"F3.wireOp",EDGE,"e5d05796-7d6c-4350-8a4e-d55f5ade2f77"),sQuery(id+"F3.wireOp",EDGE,"77b1164c-8dd4-4680-b616-ac151a422eb2"),sQuery(id+"F3.wireOp",EDGE,"ec0798b8-0fbb-49ea-9766-39d2ee0936b0"),sQuery(id+"F3.wireOp",EDGE,"c4af6478-2a03-47a6-862f-c0c71886b8a3"),sQuery(id+"F3.wireOp",EDGE,"1912a38f-fa28-45c6-ab33-84cac2787056"),sQuery(id+"F3.wireOp",EDGE,"5d79fa95-f66d-4d2b-923b-4d54735f1fbd"),sQuery(id+"F3.wireOp",EDGE,"2db7aef4-a710-4bcf-9c1c-a8a87719953d"),sQuery(id+"F3.wireOp",EDGE,"183449de-345c-4115-9bca-43a403e62dbd"),sQuery(id+"F3.wireOp",EDGE,"e3ac8c9b-cab5-44b0-ad81-0e2b680c384a"),sQuery(id+"F3.wireOp",EDGE,"92e85db6-f458-41f6-a9a1-1e1a1a7e7809"),sQuery(id+"F3.wireOp",EDGE,"f0dbb46f-43a9-447b-9c75-8dfc9b95470d"),sQuery(id+"F3.wireOp",EDGE,"4b73f5f6-f769-4414-bdba-7d253e58fff4"),sQuery(id+"F3.wireOp",EDGE,"a88669dc-35b3-46bb-964f-c9bf6c4ab898"),sQuery(id+"F3.wireOp",EDGE,"2c559bae-f38f-4377-91e6-3c9de70acf11"),sQuery(id+"F3.wireOp",EDGE,"c1caf99b-adaa-42fe-a319-8cbcd819cf89"),sQuery(id+"F3.wireOp",EDGE,"54b04dd4-0ec4-4956-b19c-1141095738e3"),sQuery(id+"F3.wireOp",EDGE,"098f7a84-b7b8-4879-b21a-5c38879e4110"),sQuery(id+"F3.wireOp",EDGE,"b406a8e6-a226-4f3d-ac30-e4d06e4dac62"),sQuery(id+"F3.wireOp",EDGE,"36f95d1d-68ce-4231-ad71-3960c85e5915"),sQuery(id+"F3.wireOp",EDGE,"dc12cad8-2eed-454e-aa74-30099b1c9064"),sQuery(id+"F3.wireOp",EDGE,"4c78a4fd-cd81-43d6-85d6-6e4d3fbc1e98"),sQuery(id+"F3.wireOp",EDGE,"ee9e30de-787b-4e8f-b425-43a8e9289f81"),sQuery(id+"F3.wireOp",EDGE,"2518a3a4-c96b-4463-8704-0b71c65c60d2"),sQuery(id+"F3.wireOp",EDGE,"c9129a67-398c-4e37-92cb-2d54ff2e2e82"),sQuery(id+"F3.wireOp",EDGE,"d429d547-9f5b-42c6-bcca-effad2fa908f"),sQuery(id+"F3.wireOp",EDGE,"99d16e94-b2b3-43d5-9c7b-7bd463994dcb"),sQuery(id+"F3.wireOp",EDGE,"32993909-9a70-47ee-9097-89fff220f839"),sQuery(id+"F3.wireOp",EDGE,"6eabbeed-9496-4825-b168-63782a34f495"),sQuery(id+"F3.wireOp",EDGE,"f74987e3-8e60-4a5b-857f-839ae8aaf0cf"),sQuery(id+"F3.wireOp",EDGE,"1c218c86-035d-4441-93c0-9621d3297c3a"),sQuery(id+"F3.wireOp",EDGE,"0133f513-4b11-4cc4-b075-4625e9591e41"),sQuery(id+"F3.wireOp",EDGE,"fe921ad4-a8f5-4772-9aeb-350aca2e8948"),sQuery(id+"F3.wireOp",EDGE,"bfde0a4f-3cec-4f8e-8a23-dd1441b34c2b"),sQuery(id+"F3.wireOp",EDGE,"b41521ff-c5df-4b64-83ed-5e7635cf4438"),sQuery(id+"F3.wireOp",EDGE,"ed692599-6bbb-4379-8e89-ea326a0a0f87"),sQuery(id+"F3.wireOp",EDGE,"a98451c0-d76c-436e-99f9-a3fe9c8430a4"),sQuery(id+"F3.wireOp",EDGE,"561965b2-3050-4f49-9305-d98a2b852bbe"),sQuery(id+"F3.wireOp",EDGE,"e13dfa59-48e6-4b4e-94b9-1fc5254b0f2e"),sQuery(id+"F3.wireOp",EDGE,"0354e106-253a-4bfa-b5b7-b09cd0f2f6c0"),sQuery(id+"F3.wireOp",EDGE,"8df1dcc8-d00a-4777-85fd-8af8e9830bd1"),sQuery(id+"F3.wireOp",EDGE,"26ce3762-0d1a-4b81-9a23-debcfc24da1c"),sQuery(id+"F3.wireOp",EDGE,"3e900f8f-3ffb-4e32-b536-61fea2f3e30a"),sQuery(id+"F3.wireOp",EDGE,"4a1b5445-5559-461f-b6f1-b4cd9b95ea10")])]});
            var Q4;
            Q4=makeQuery(id+"F1.opRevolve","SWEPT_BODY",BODY,{"disambiguationData":[OSD([sQuery(id+"F0.wireOp",EDGE,"E0"),sQuery(id+"F0.wireOp",EDGE,"E1")])]});
            var Q5;
            Q5=qCreatedBy(makeId("Origin.pointOp"),VERTEX);
            transform(context, id + "F5", {"entities" : qUnion([Q0, Q1, Q2, Q3, Q4]), "transformType" : TransformType.SCALE_UNIFORMLY, "scale" : 0.03, "scalePoint" : qUnion([Q5]), "makeCopy" : false});
        }
        {
            var Q0;
            Q0=qCreatedBy(makeId("Top.planeOp"),FACE);
            var sketch = newSketch(context, id + "F6", { "sketchPlane" : qUnion([Q0])});
            skLineSegment(sketch, "E150", {"start": v(0, 15) * mm, "end": v(0, -15) * mm});
            skArc(sketch, "E151", {"start": v(0, 15) * mm, "mid": v(-15, 0) * mm, "end": v(0, -15) * mm});
            skArc(sketch, "E152", {"start": v(0, 10.25) * mm, "mid": v(-10.25, 0) * mm, "end": v(0, -10.25) * mm});
            skArc(sketch, "E153", {"start": v(0, 7) * mm, "mid": v(-7, 0) * mm, "end": v(0, -7) * mm});
            skSolve(sketch);
        }
        {
            var Q0;
            {var subQ0=sQuery(id+"F6.wireOp",EDGE,"E151");Q0=makeQuery(id+"F6.imprint","IMPRINT",FACE,{"disambiguationData":[TD([[makeQuery(id+"F6.imprint","IMPRINT",EDGE,{"derivedFrom":subQ0}),1.0]])]});}
            var Q1;
            {var subQ0=sQuery(id+"F6.wireOp",EDGE,"E153");Q1=makeQuery(id+"F6.imprint","IMPRINT",FACE,{"disambiguationData":[TD([[makeQuery(id+"F6.imprint","IMPRINT",EDGE,{"derivedFrom":subQ0}),1.0]])]});}
            var Q2;
            Q2=sQuery(id+"F6.wireOp",EDGE,"E150");
            revolve(context, id + "F7", {"operationType" : NewBodyOperationType.REMOVE, "entities" : qUnion([Q0, Q1]), "axis" : qUnion([Q2]), "revolveType" : RevolveType.FULL});
        }
        {
            var Q0;
            Q0=makeQuery(id+"F1.opRevolve","SWEPT_BODY",BODY,{"disambiguationData":[OSD([sQuery(id+"F0.wireOp",EDGE,"E0"),sQuery(id+"F0.wireOp",EDGE,"E1")])]});
            var Q1;
            Q1=sQuery(id+"F0.wireOp",VERTEX,"E1.center");
            transform(context, id + "F8", {"entities" : qUnion([Q0]), "transformType" : TransformType.SCALE_UNIFORMLY, "scale" : 1.4, "scalePoint" : qUnion([Q1]), "makeCopy" : false});
        }
        {
            var Q0;
            Q0=qCreatedBy(makeId("Front.planeOp"),FACE);
            var sketch = newSketch(context, id + "F9", { "sketchPlane" : qUnion([Q0])});
            skCircle(sketch, "E154", {"center": v(0, -5.12) * mm, "radius": 2 * mm});
            skSolve(sketch);
        }
        {
            var Q0;
            Q0=qSketchRegion(id+"F9",true);
            extrude(context, id + "F10", {"entities" : qUnion([Q0]), "operationType" : NewBodyOperationType.REMOVE, "oppositeDirection" : true, "depth" : 25 * mm});
        }
        {
            var Q0;
            Q0=qCreatedBy(makeId("Top.planeOp"),FACE);
            var sketch = newSketch(context, id + "F11", { "sketchPlane" : qUnion([Q0])});
            skLineSegment(sketch, "E155", {"start": v(-46.39, 0) * mm, "end": v(52, 0) * mm});
            skSolve(sketch);
        }
        {
            var Q0;
            Q0=sQuery(id+"F11.wireOp",EDGE,"E155");
            cPlane(context, id + "F12", {"entities" : qUnion([Q0]), "cplaneType" : CPlaneType.LINE_ANGLE, "offset" : 25 * mm, "angle" : 40 * degree, "width" : 150 * mm, "height" : 150 * mm});
        }
        {
            var Q0;
            Q0=qCreatedBy(id+"F12.planeOp",FACE);
            var sketch = newSketch(context, id + "F13", { "sketchPlane" : qUnion([Q0])});
            skText(sketch, "E156", { "text": "Building", "fontName": "OpenSans-Italic.ttf"});
            const initialGuessF13  = {"E156": [-0.01026, -0.003, 1, 0, 0.004]};
            skSetInitialGuess(sketch, initialGuessF13);
            skSolve(sketch);
        }
        {
            var Q0;
            Q0=qCreatedBy(makeId("Right.planeOp"),FACE);
            var sketch = newSketch(context, id + "F14", { "sketchPlane" : qUnion([Q0])});
            skArc(sketch, "E157", {"start": v(0, -14.25) * mm, "mid": v(-14.25, 0) * mm, "end": v(0, 14.25) * mm});
            skLineSegment(sketch, "E158", {"start": v(0, 14.25) * mm, "end": v(0, -14.25) * mm});
            skSolve(sketch);
        }
        {
            var Q0;
            Q0=makeQuery(id+"F14.imprint","IMPRINT",FACE,{"disambiguationData":[TD([[makeQuery(id+"F14.imprint","IMPRINT",EDGE,{"derivedFrom":sQuery(id+"F14.wireOp",EDGE,"E157")}),-1.0]])]});
            var Q1;
            Q1=sQuery(id+"F14.wireOp",EDGE,"E157");
            var Q2;
            Q2=sQuery(id+"F14.wireOp",EDGE,"E158");
            revolve(context, id + "F15", {"bodyType" : ToolBodyType.SURFACE, "operationType" : NewBodyOperationType.ADD, "entities" : qUnion([Q0]), "surfaceEntities" : qUnion([Q1]), "axis" : qUnion([Q2]), "revolveType" : RevolveType.FULL});
        }
        {
            var Q0;
            Q0 = qSketchRegion(id + "F13", true);
            var Q1;
            Q1=makeQuery(id+"F15.opRevolve","SWEPT_FACE",FACE,{"disambiguationData":[OSD([sQuery(id+"F14.wireOp",EDGE,"E157")])]});
            extrude(context, id + "F16", {"entities" : qUnion([Q0]), "operationType" : NewBodyOperationType.ADD, "endBound" : BoundingType.UP_TO_SURFACE, "depth" : 25 * mm, "endBoundEntityFace" : qUnion([Q1]), "offsetDistance" : 25 * mm});
        }
    });
